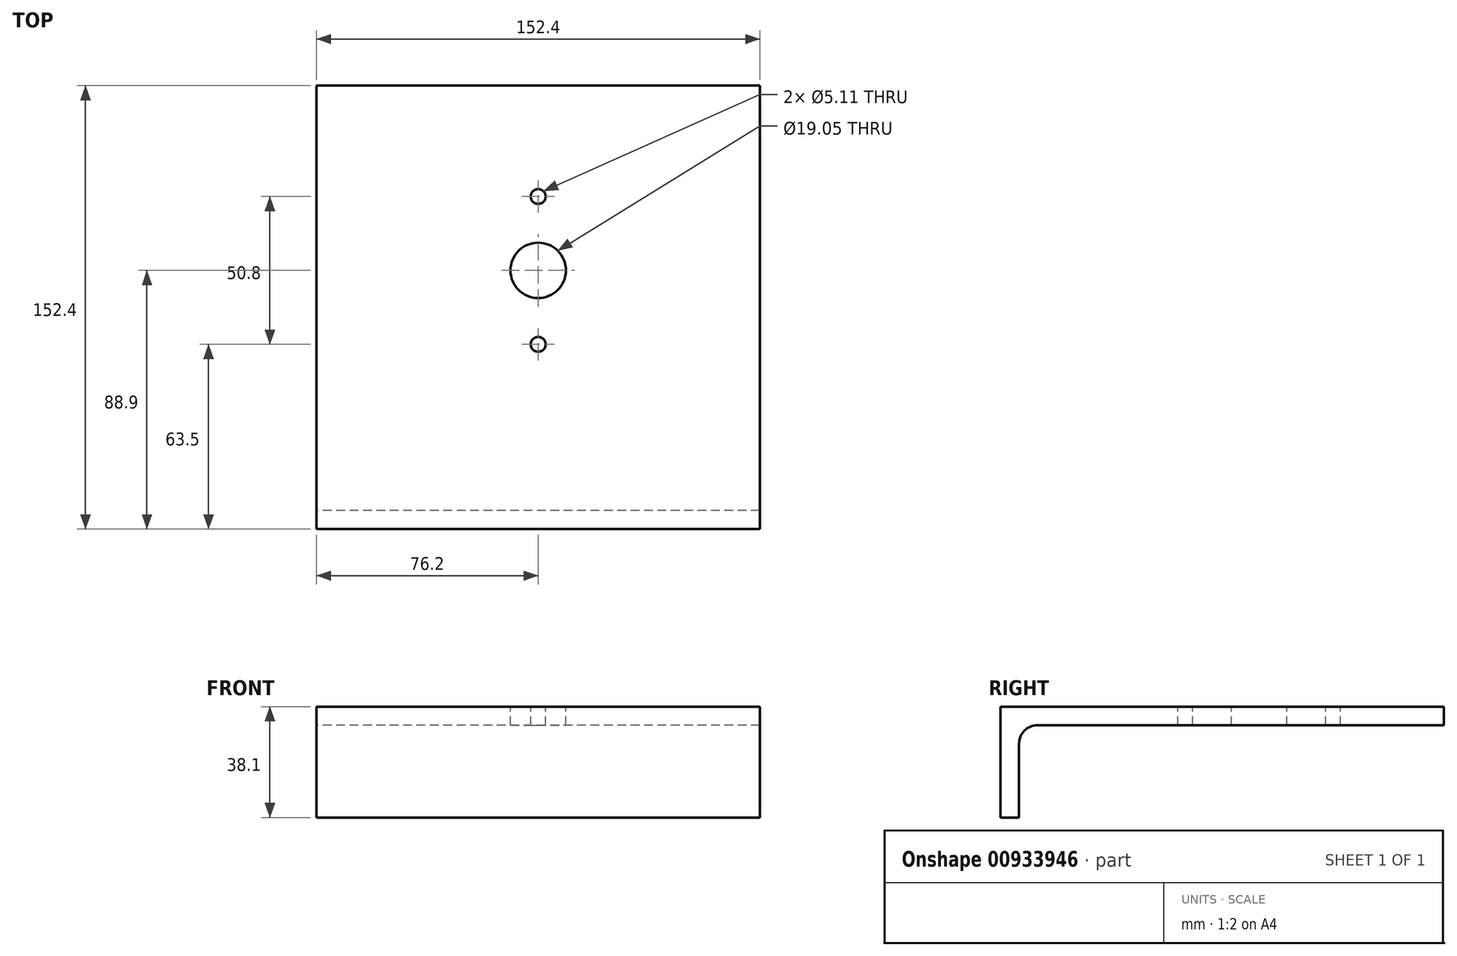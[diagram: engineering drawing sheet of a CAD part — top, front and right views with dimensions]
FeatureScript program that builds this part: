
annotation { "Feature Type Name" : "Feature", "Feature Type Description" : "" }
export const myFeature = defineFeature(function(context is Context, id is Id, definition is map)
    precondition{}
    {
        {
            var Q0;
            Q0=qCreatedBy(makeId("Right.planeOp"),FACE);
            var sketch = newSketch(context, id + "F0", { "sketchPlane" : qUnion([Q0])});
            skLineSegment(sketch, "E0", {"start": v(0, 0) * mm, "end": v(152.4, 0) * mm});
            skLineSegment(sketch, "E1", {"start": v(152.4, 0) * mm, "end": v(152.4, -6.35) * mm});
            skLineSegment(sketch, "E2", {"start": v(152.4, -6.35) * mm, "end": v(12.7, -6.35) * mm});
            skLineSegment(sketch, "E3", {"start": v(6.35, -12.7) * mm, "end": v(6.35, -38.1) * mm});
            skLineSegment(sketch, "E4", {"start": v(6.35, -38.1) * mm, "end": v(0, -38.1) * mm});
            skLineSegment(sketch, "E5", {"start": v(0, -38.1) * mm, "end": v(0, 0) * mm});
            skPoint(sketch, "E6.visualSharp", {"position": v(6.35, -6.35) * mm});
            skArc(sketch, "E6.filletArc", {"start": v(12.7, -6.35) * mm, "mid": v(8.2, -8.2) * mm, "end": v(6.35, -12.7) * mm});
            skSolve(sketch);
        }
        {
            var Q0;
            Q0 = qSketchRegion(id + "F0", true);
            extrude(context, id + "F1", {"entities" : qUnion([Q0]), "endBound" : BoundingType.SYMMETRIC, "depth" : 152.4 * mm, "offsetDistance" : 25.4 * mm});
        }
        {
            var Q0;
            Q0=qCreatedBy(makeId("Top.planeOp"),FACE);
            var sketch = newSketch(context, id + "F2", { "sketchPlane" : qUnion([Q0])});
            skCircle(sketch, "E7", {"center": v(0, 88.9) * mm, "radius": 9.53 * mm});
            skCircle(sketch, "E8", {"center": v(0, 114.3) * mm, "radius": 2.55 * mm});
            skCircle(sketch, "E9", {"center": v(0, 63.5) * mm, "radius": 2.55 * mm});
            skSolve(sketch);
        }
        {
            var Q0;
            Q0 = qSketchRegion(id + "F2", true);
            extrude(context, id + "F3", {"entities" : qUnion([Q0]), "operationType" : NewBodyOperationType.REMOVE, "endBound" : BoundingType.THROUGH_ALL, "oppositeDirection" : true, "depth" : 25.4 * mm, "offsetDistance" : 25.4 * mm});
        }
    });
